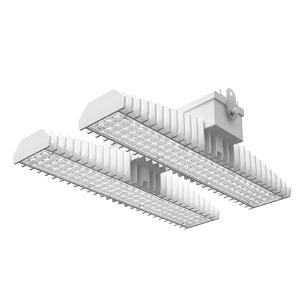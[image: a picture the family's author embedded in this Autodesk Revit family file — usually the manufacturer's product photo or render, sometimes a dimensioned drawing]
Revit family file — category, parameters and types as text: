
# Revit family: 3f_filippi_-_3f_lem_ho_concentrato_3f_filippi_-_58960_a0811_-_3f_lem_2_ho_led_140_cr_conc___vt_c2a0
name_source: partatom
category: Lighting Fixtures
units: mm (PartAtom-declared; Revit-internal decimal feet)

## family parameters
Cut with Voids When Loaded = No
Host = Face
Light Source = No
Part Type = Normal
Room Calculation Point = No
Round Connector Dimension = Use Diameter
Shared = No

## types (1)
- 3F Filippi - 3F LEM HO Concentrato (1 x LED, 20166 lm, 138 W, 4000 K)
    Apparent Load = 138 VA
    Approval mark = CE
    CIE Flux Codes = 83 96 99 100 100
    Color Rendering = 80
    Color Temperature = 4000 K
    Control Gear = Electronic ballast
    Default Elevation = 1800 mm
    Description = Industrial luminaire with high light output and high luminous efficiency designed with the most innovative technologies for environments with temperature up to 55°C.

ILLUMINOTECHNICAL
Luminous efficiency 100% (DLOR 99%, ULOR 1%).
Initial luminous flux of the luminaire 20166 lm.
Direct symmetric narrow distribution: the illuminated area has a elliptical shape.
Installation Interdistance Transv.D = 0.52 x hu - Long.D = 1.16 x hu.
Tabular UGR (CIE 117 - 4H-8H; S=0.25H; 70/50/20): RUG 17.4 - 21.3.
Beam angle: 31° - 73°.
Luminous efficacy 146 lm/W.
Lifetime (L93/B10): 30000 h. (tq+25°C)
Lifetime (L90/B10): 50000 h. (tq+25°C)
Lifetime (L85/B10): 80000 h. (tq+25°C)
Lifetime (L80/B10): 100000 h. (tq+25°C)
Lifetime (L85/B10): 50000 h. (tq+55°C)
Sudden decreased luminous flux after 50000 hours: 0% (C0).
Photobiological safety in compliance with IEC/TR 62778: RG0 risk exempt, (IEC 62471).
In compliance with IEC/EN 62722-2-1 - IEC/EN 62717 standards.

SOURCE
2 Mid-Power linear LED modules 70W/840.
Energy efficiency class (UE 2019/2020 - UE 2019/2015): C.
CIE 13.3 Colour rendering index: CRI >80 (R9 <50%).
IES TM-30 Fidelity Index: Rf = 84 Rg = 95.
CCT nominal colour temperature 4000 K.
Colour initial tolerance (MacAdam): SDCM 3.

MECHANICAL
Passive modular heatsinks in die-casted aluminium, painted in white colour.
To optimize the thermal management of the LED module, the heatsinks are oversized and provided with self-cleaning of cooling fins.
Wiring body in aluminium and galvanised steel anchored solidly to the sinks and thermally separated.
3F Lens lenses with high luminous efficiency, transparent methacrylate (PMMA), fixed to the LED modules.
Fixing brackets in stainless steel.
Luminaire with limited surface temperature. - D - (EN 60598-2-24)
Dimensions: 470x542 mm, height 133 mm. Weight 10.054 kg.
IP65 protection degree.
Mechanical strength to impacts IK06 (1 joule).
Glow-wire test resistance 650°C.

ELECTRICAL
Halogen Free electronic wiring 230V-50/60Hz, power factor 0.97, THD <25%, constant output current, class I, 1 driver.
Power of the luminaire 138 W.
ENEC - CE.
SAFE FLICKER: PstLM=<1 and SVM=<0.4 (IEC TR 61547-1 and IEC TR 63158), to ensure a more comfortable and safe light.
Luminaire compliant with EN 60598-2-22 for power supply from a centralised emergency system CPSS (Central Power Supply System), not incorporated in the luminaire - high risk areas excluded. The default power and flux are 100% in AC and 100% in DC.
Ambient temperature from -30°C to +55°C.
Temperature class T6 max 85°C.
Quick connection via M20 3P connector with 9-13 mm tightening range.
Power unit positioned on a separate compartment by the LED module to ensure optimum temperatures of cabling components, to be inspectable and maintainable.
Relative humidity UR: <85%.

INSTALLATION
Ceiling / Suspended / Wall.
All accessories dedicated to this product are available on the Catalog and on our website www.3F-Filippi.com.

ACCESSORIES
A0811 - VT transparent glass, tempered, not flammable, with sealing gasket.
One required for each light module. The pack contains 10 pieces.

APPLICATIONS
In commercial environments, exhibition and industrial areas, stores, open areas or with shelves.
Environments in which it is necessary a total protection against falling fragments (eg environments with foodstuffs or machines with moving parts or with extreme temperature changes), use luminaires with polycarbonate lenses.

WARNING
Fixture not suitable for cold stores with an ambient temperature <0°C and/or relative humidity >85%.
Luminaire designed for disposal/recycling at end-of-life.
Replaceable (LED only) light source by a professional. Replaceable control gear by a professional.
    Height = 133 mm  [stored 0.436352 ft]
    Lamp = 1 x LED
    Lamp Light Flux = 20166 lm
    Lamp Power = 138 W
    Lamp count = 1
    Length = 470 mm
    Lifetime = 50000 h
    Luminous efficacy = 146 lm/W
    Manufacturer = 3F Filippi
    ModVariant = No
    Model = 3F Filippi - 58960+A0811 - 3F LEM 2 HO LED 140 CR CONC + VT
    Mounting Place = Ceiling
    Mounting Type = Pendant
    Number of Poles = 1
    OnlyDefault = Yes
    Power Factor = 1
    Product Name = 3F Filippi - 3F LEM HO Concentrato
    Product group = pendant luminaire
    ProductGroupID = 9
    Protection Class = Protection class I
    Protection Degree = IP 65
    RLX_Detail_Level = 1
    RLX_Emergency_Light_Flux = 0 lm
    RLX_Emergency_Type = 0
    RLX_Emergency_Type_DB = No
    RlxData = <blob elided: 102201 chars, md5=8f018359>
    Socket = socket
    Standby Power = 0 W
    System Light Flux = 20166 lm
    System Power = 138 W
    Type Comments = Product without accessories
    Type Image = 3f_filippi_-_lem_2__a0811.jpg
    URL = http://relux.com
    VarID = ---
    Voltage = 0 V
    Weight = 0.00 kg
    Width = 542 mm

note: [stored X ft] marks values corroborated as IEEE doubles in the binary element streams (Revit-internal decimal feet)

## geometry (parser evidence)
native form markers: Blend x4, Sweep x11
no freeform markers — native parametric forms only
